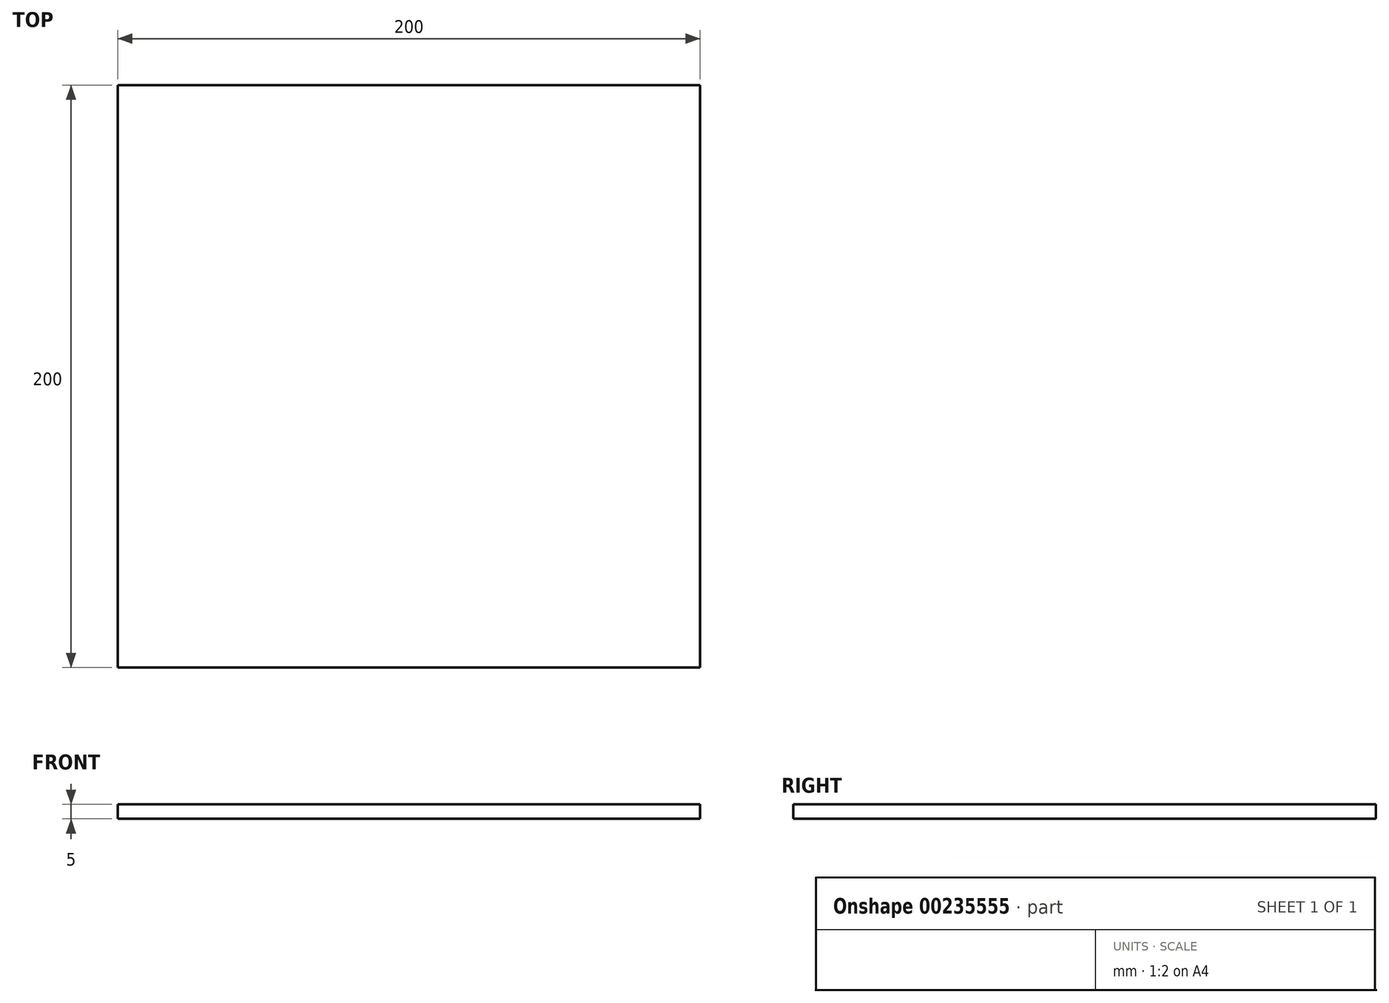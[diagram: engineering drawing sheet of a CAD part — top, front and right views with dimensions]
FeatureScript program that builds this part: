
annotation { "Feature Type Name" : "Feature", "Feature Type Description" : "" }
export const myFeature = defineFeature(function(context is Context, id is Id, definition is map)
    precondition{}
    {
        {
            var Q0;
            Q0=qCreatedBy(makeId("Top.planeOp"),FACE);
            var sketch = newSketch(context, id + "F0", { "sketchPlane" : qUnion([Q0])});
            skLineSegment(sketch, "E0.bottom", {"start": v(100, -100) * mm, "end": v(-100, -100) * mm});
            skLineSegment(sketch, "E0.top", {"start": v(100, 100) * mm, "end": v(-100, 100) * mm});
            skLineSegment(sketch, "E0.left", {"start": v(100, -100) * mm, "end": v(100, 100) * mm});
            skLineSegment(sketch, "E0.right", {"start": v(-100, -100) * mm, "end": v(-100, 100) * mm});
            skPoint(sketch, "E0.middle", {"position": v(0, 0) * mm});
            skSolve(sketch);
        }
        {
            var Q0;
            Q0 = qSketchRegion(id + "F0", true);
            extrude(context, id + "F1", {"entities" : qUnion([Q0]), "depth" : 5 * mm});
        }
    });
